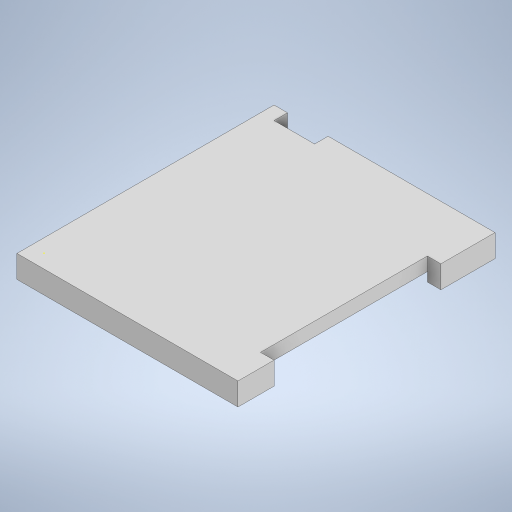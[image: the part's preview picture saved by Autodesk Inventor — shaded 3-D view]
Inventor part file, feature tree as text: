
AUTODESK INVENTOR PART (.ipt)
format: ipt  version: 2023 (Build 270158000, 158)  size: 242,176 bytes
history: native  units: mm
features: sketch x4, extrude x2
ambient origin geometry x8: Origin, YZ Plane, XZ Plane, XY Plane, X Axis, Y Axis, Z Axis, Center Point
bodies: Solid1 (feature_tree)
feature tree (6):
  sketch  "Sketch1"  dims[d0=43.0mm d1=51.0mm]
  sketch  "Sketch2"  dims[d2=3.0mm d3=9.0mm]
  extrude  "Extrusion1"  Depth=51.0mm
  extrude  "Extrusion2"  Depth=9.0mm
  sketch  "Sketch4"  dims[d5=5.0mm d6=3.0mm d7=3.0mm d8=3.0mm d9=3.0mm d10=3.0mm d11=34.0mm d12=5.0mm d13=0.0mm d14=3.0mm d15=0.0mm]
  sketch  "Sketch3"  dims[d4=3.0mm]
